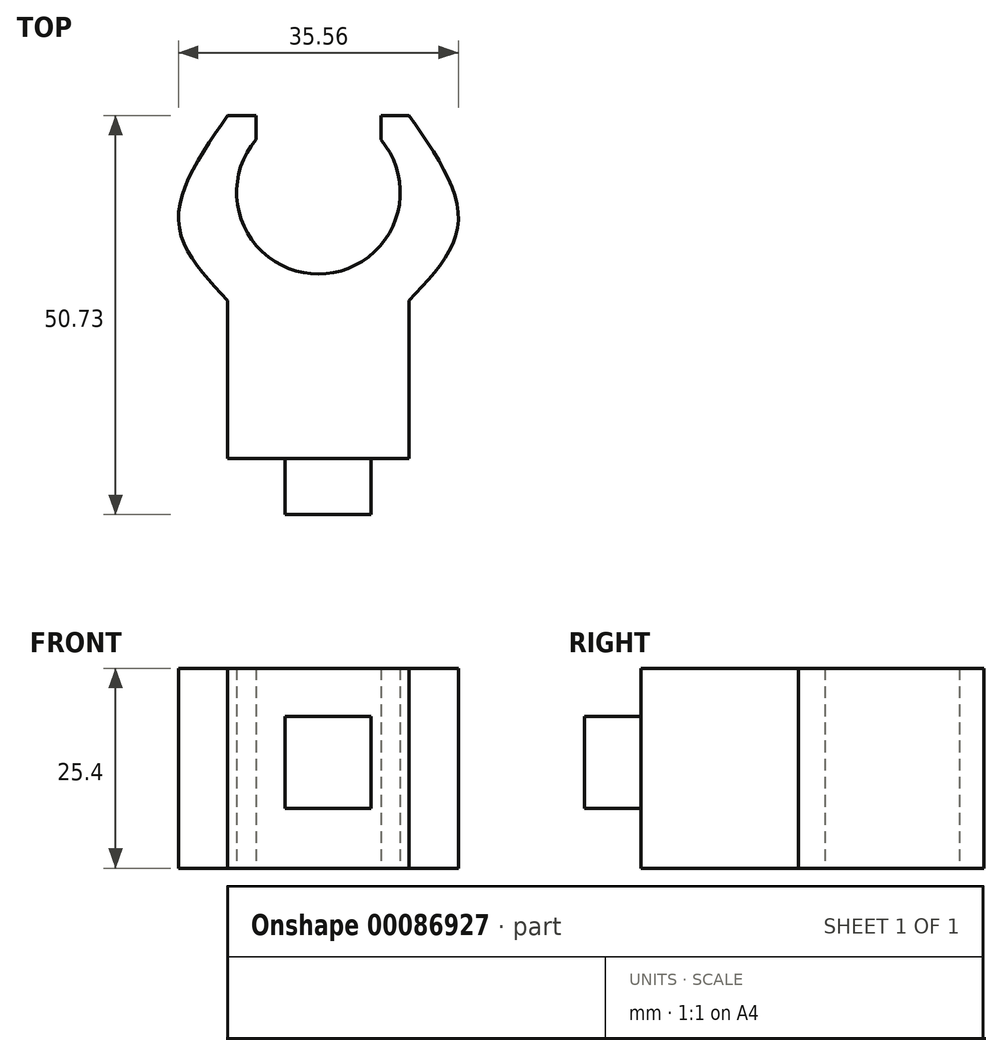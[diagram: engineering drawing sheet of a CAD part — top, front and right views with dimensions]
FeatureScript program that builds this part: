
annotation { "Feature Type Name" : "Feature", "Feature Type Description" : "" }
export const myFeature = defineFeature(function(context is Context, id is Id, definition is map)
    precondition{}
    {
        {
            var Q0;
            Q0=qCreatedBy(makeId("Top.planeOp"),FACE);
            var sketch = newSketch(context, id + "F0", { "sketchPlane" : qUnion([Q0])});
            skLineSegment(sketch, "E0.top", {"start": v(-42.4, -11.45) * mm, "end": v(-19.33, -11.45) * mm});
            skLineSegment(sketch, "E0.left", {"start": v(-42.4, 8.6) * mm, "end": v(-42.4, -11.45) * mm});
            skLineSegment(sketch, "E0.right", {"start": v(-19.33, 8.6) * mm, "end": v(-19.33, -11.45) * mm});
            skPoint(sketch, "E1.2.internal.snap0", {"position": v(-19.33, -1.42) * mm});
            skFitSpline(sketch, "E1", {"points": [v(-19.33, 8.6) * mm, v(-13.1, 18.63) * mm, v(-19.33, 32.12) * mm], "startDerivative": vector(19.13, 20.28) * mm, "endDerivative": vector(-18.4, 26.63) * mm});
            skFitSpline(sketch, "E2.MirrorCS", {"points": [v(-42.4, 8.6) * mm, v(-48.63, 18.63) * mm, v(-42.4, 32.12) * mm], "startDerivative": vector(-19.13, 20.28) * mm, "endDerivative": vector(18.4, 26.63) * mm});
            skLineSegment(sketch, "E3", {"start": v(-42.4, 32.12) * mm, "end": v(-38.79, 32.12) * mm});
            skLineSegment(sketch, "E4.MirrorCS", {"start": v(-19.33, 32.12) * mm, "end": v(-22.93, 32.12) * mm});
            skLineSegment(sketch, "E5", {"start": v(-38.79, 32.12) * mm, "end": v(-38.79, 29.06) * mm});
            skLineSegment(sketch, "E6", {"start": v(-22.93, 32.12) * mm, "end": v(-22.93, 29.06) * mm});
            skArc(sketch, "E7", {"start": v(-38.79, 29.06) * mm, "mid": v(-30.86, 11.96) * mm, "end": v(-22.93, 29.06) * mm});
            skSolve(sketch);
        }
        {
            var Q0;
            Q0=makeQuery(id+"F0.imprint","IMPRINT",FACE,{"disambiguationData":[TD([[makeQuery(id+"F0.imprint","IMPRINT",EDGE,{"derivedFrom":sQuery(id+"F0.wireOp",EDGE,"E0.top")}),1.0]])]});
            extrude(context, id + "F1", {"entities" : qUnion([Q0]), "depth" : 25.4 * mm});
        }
        {
            var Q0;
            Q0=makeQuery(id+"F1.opExtrude","SWEPT_FACE",FACE,{"disambiguationData":[OSD([sQuery(id+"F0.wireOp",EDGE,"E0.top")])]});
            var sketch = newSketch(context, id + "F2", { "sketchPlane" : qUnion([Q0])});
            skSolve(sketch);
        }
        {
            var Q0;
            {var subQ0=sQuery(id+"F0.wireOp",EDGE,"E0.top");Q0=makeQuery(id+"F2.imprint","IMPRINT",FACE,{"disambiguationData":[TD([[makeQuery(id+"F2.imprint","IMPRINT",EDGE,{"derivedFrom":makeQuery(id+"F1.opExtrude","CAP_EDGE",EDGE,{"disambiguationData":[OSD([subQ0])],"isStart":true})}),1.0]])]});}
            var sketch = newSketch(context, id + "F3", { "sketchPlane" : qUnion([Q0])});
            skLineSegment(sketch, "E8.bottom", {"start": v(-35.13, 19.28) * mm, "end": v(-24.18, 19.28) * mm});
            skLineSegment(sketch, "E8.top", {"start": v(-35.13, 7.62) * mm, "end": v(-24.18, 7.62) * mm});
            skLineSegment(sketch, "E8.left", {"start": v(-35.13, 19.28) * mm, "end": v(-35.13, 7.62) * mm});
            skLineSegment(sketch, "E8.right", {"start": v(-24.18, 19.28) * mm, "end": v(-24.18, 7.62) * mm});
            skSolve(sketch);
        }
        {
            var Q0;
            Q0=makeQuery(id+"F3.imprint","IMPRINT",FACE,{"disambiguationData":[TD([[makeQuery(id+"F3.imprint","IMPRINT",EDGE,{"derivedFrom":sQuery(id+"F3.wireOp",EDGE,"E8.bottom")}),-1.0]])]});
            extrude(context, id + "F4", {"entities" : qUnion([Q0]), "operationType" : NewBodyOperationType.ADD, "depth" : 7.15 * mm});
        }
    });
